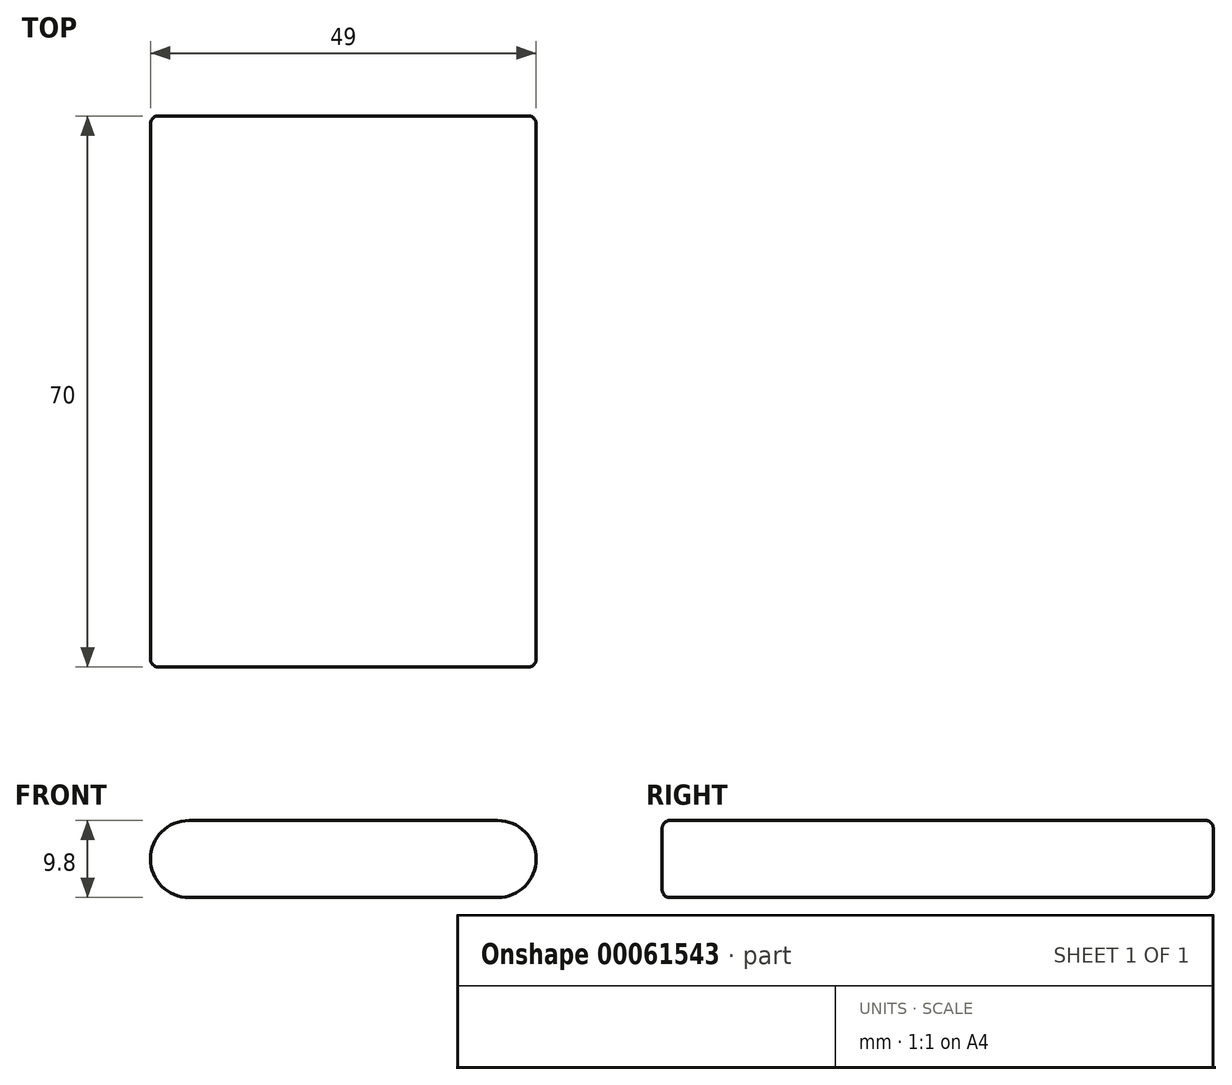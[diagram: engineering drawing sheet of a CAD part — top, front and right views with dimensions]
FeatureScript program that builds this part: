
annotation { "Feature Type Name" : "Feature", "Feature Type Description" : "" }
export const myFeature = defineFeature(function(context is Context, id is Id, definition is map)
    precondition{}
    {
        {
            var Q0;
            Q0=qCreatedBy(makeId("Front.planeOp"),FACE);
            var sketch = newSketch(context, id + "F0", { "sketchPlane" : qUnion([Q0])});
            skLineSegment(sketch, "E0.bottom", {"start": v(-51.32, 20.59) * mm, "end": v(-12.12, 20.59) * mm});
            skLineSegment(sketch, "E0.top", {"start": v(-51.32, 10.79) * mm, "end": v(-12.12, 10.79) * mm});
            skLineSegment(sketch, "E0.left", {"start": v(-56.22, 15.69) * mm, "end": v(-56.22, 15.69) * mm});
            skLineSegment(sketch, "E0.right", {"start": v(-7.22, 15.69) * mm, "end": v(-7.22, 15.69) * mm});
            skPoint(sketch, "E1.visualSharp", {"position": v(-56.22, 20.59) * mm});
            skArc(sketch, "E1.filletArc", {"start": v(-51.32, 20.59) * mm, "mid": v(-54.79, 19.15) * mm, "end": v(-56.22, 15.69) * mm});
            skPoint(sketch, "E2.visualSharp", {"position": v(-56.22, 10.79) * mm});
            skArc(sketch, "E2.filletArc", {"start": v(-56.22, 15.69) * mm, "mid": v(-54.79, 12.22) * mm, "end": v(-51.32, 10.79) * mm});
            skPoint(sketch, "E3.visualSharp", {"position": v(-7.22, 10.79) * mm});
            skArc(sketch, "E3.filletArc", {"start": v(-12.12, 10.79) * mm, "mid": v(-8.66, 12.22) * mm, "end": v(-7.22, 15.69) * mm});
            skPoint(sketch, "E4.visualSharp", {"position": v(-7.22, 20.59) * mm});
            skArc(sketch, "E4.filletArc", {"start": v(-7.22, 15.69) * mm, "mid": v(-8.66, 19.15) * mm, "end": v(-12.12, 20.59) * mm});
            skSolve(sketch);
        }
        {
            var Q0;
            Q0=makeQuery(id+"F0.imprint","IMPRINT",FACE,{"disambiguationData":[TD([[makeQuery(id+"F0.imprint","IMPRINT",EDGE,{"derivedFrom":sQuery(id+"F0.wireOp",EDGE,"E0.bottom")}),-1.0]])]});
            extrude(context, id + "F1", {"entities" : qUnion([Q0]), "depth" : 70 * mm});
        }
        {
            var Q0;
            Q0=makeQuery(id+"F1.opExtrude","CAP_EDGE",EDGE,{"disambiguationData":[OSD([sQuery(id+"F0.wireOp",EDGE,"E0.bottom")])],"isStart":false});
            var Q1;
            Q1=makeQuery(id+"F1.opExtrude","CAP_EDGE",EDGE,{"disambiguationData":[OSD([sQuery(id+"F0.wireOp",EDGE,"E1.filletArc"),sQuery(id+"F0.wireOp",EDGE,"E2.filletArc")])],"isStart":false});
            var Q2;
            Q2=makeQuery(id+"F1.opExtrude","CAP_EDGE",EDGE,{"disambiguationData":[OSD([sQuery(id+"F0.wireOp",EDGE,"E0.top")])],"isStart":false});
            var Q3;
            Q3=makeQuery(id+"F1.opExtrude","CAP_EDGE",EDGE,{"disambiguationData":[OSD([sQuery(id+"F0.wireOp",EDGE,"E3.filletArc"),sQuery(id+"F0.wireOp",EDGE,"E4.filletArc")])],"isStart":false});
            var Q4;
            Q4=makeQuery(id+"F1.opExtrude","CAP_EDGE",EDGE,{"disambiguationData":[OSD([sQuery(id+"F0.wireOp",EDGE,"E1.filletArc"),sQuery(id+"F0.wireOp",EDGE,"E2.filletArc")])],"isStart":true});
            var Q5;
            Q5=makeQuery(id+"F1.opExtrude","CAP_EDGE",EDGE,{"disambiguationData":[OSD([sQuery(id+"F0.wireOp",EDGE,"E0.bottom")])],"isStart":true});
            var Q6;
            Q6=makeQuery(id+"F1.opExtrude","CAP_EDGE",EDGE,{"disambiguationData":[OSD([sQuery(id+"F0.wireOp",EDGE,"E0.top")])],"isStart":true});
            var Q7;
            Q7=makeQuery(id+"F1.opExtrude","CAP_FACE",FACE,{"disambiguationData":[OSD([sQuery(id+"F0.wireOp",EDGE,"E0.bottom"),sQuery(id+"F0.wireOp",EDGE,"E0.top"),sQuery(id+"F0.wireOp",EDGE,"E1.filletArc"),sQuery(id+"F0.wireOp",EDGE,"E2.filletArc"),sQuery(id+"F0.wireOp",EDGE,"E3.filletArc"),sQuery(id+"F0.wireOp",EDGE,"E4.filletArc")])],"isStart":true});
            fillet(context, id + "F2", {"entities" : qUnion([Q0, Q1, Q2, Q3, Q4, Q5, Q6, Q7]), "radius" : 1 * mm, "tangentPropagation" : true, "allowEdgeOverflow" : false});
        }
    });
